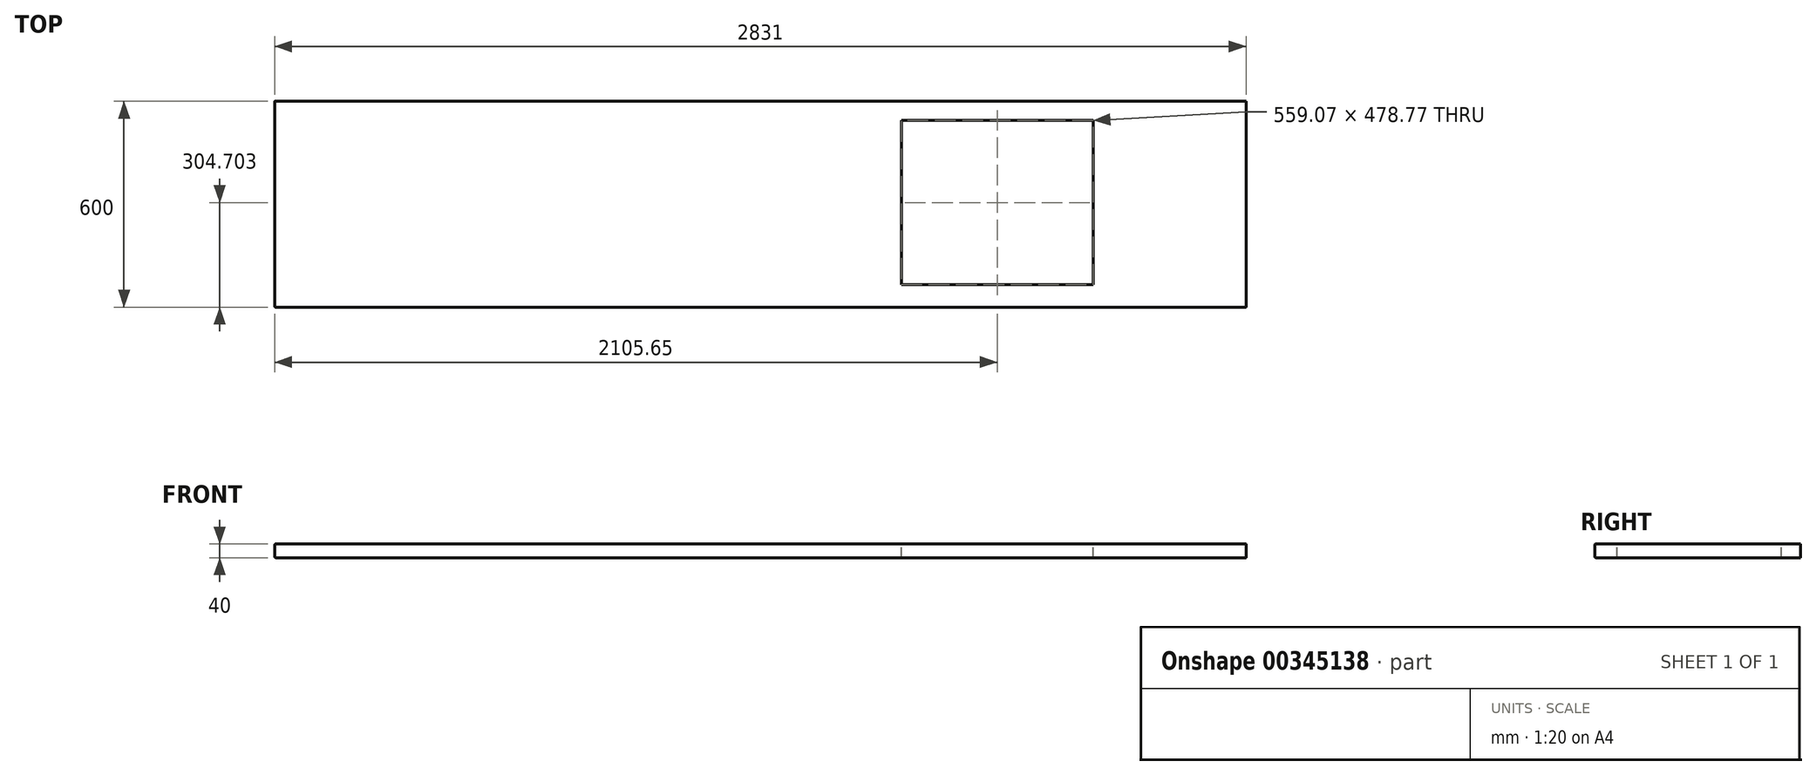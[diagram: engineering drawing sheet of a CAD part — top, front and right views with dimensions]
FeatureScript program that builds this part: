
annotation { "Feature Type Name" : "Feature", "Feature Type Description" : "" }
export const myFeature = defineFeature(function(context is Context, id is Id, definition is map)
    precondition{}
    {
        {
            var Q0;
            Q0=qCreatedBy(makeId("Top.planeOp"),FACE);
            var sketch = newSketch(context, id + "F0", { "sketchPlane" : qUnion([Q0])});
            skLineSegment(sketch, "E0.bottom", {"start": v(0, 0) * mm, "end": v(45.3, 0) * mm});
            skLineSegment(sketch, "E0.top", {"start": v(0, -35.35) * mm, "end": v(45.3, -35.35) * mm});
            skLineSegment(sketch, "E0.left", {"start": v(0, 0) * mm, "end": v(0, -35.35) * mm});
            skLineSegment(sketch, "E0.right", {"start": v(45.3, 0) * mm, "end": v(45.3, -35.35) * mm});
            skSolve(sketch);
        }
        {
            var Q0;
            Q0=makeQuery(id+"F0.imprint","IMPRINT",FACE,{"disambiguationData":[TD([[makeQuery(id+"F0.imprint","IMPRINT",EDGE,{"derivedFrom":sQuery(id+"F0.wireOp",EDGE,"E0.bottom")}),-1.0]])]});
            extrude(context, id + "F1", {"entities" : qUnion([Q0]), "depth" : 40 * mm});
        }
        {
            var Q0;
            Q0=makeQuery(id+"F1.opExtrude","SWEPT_FACE",FACE,{"disambiguationData":[OSD([sQuery(id+"F0.wireOp",EDGE,"E0.left")])]});
            extrude(context, id + "F2", {"entities" : qUnion([Q0]), "operationType" : NewBodyOperationType.ADD, "oppositeDirection" : true, "depth" : 2900 * mm});
        }
        {
            var Q0;
            {var subQ0=sQuery(id+"F0.wireOp",EDGE,"E0.bottom");Q0=makeQuery(id+"F2.boolean.opBoolean","MERGE",FACE,{"derivedFrom":[makeQuery(id+"F1.opExtrude","SWEPT_FACE",FACE,{"disambiguationData":[OSD([subQ0])]}),makeQuery(id+"F2.opExtrude","SWEPT_FACE",FACE,{"disambiguationData":[OSD([subQ0,sQuery(id+"F0.wireOp",EDGE,"E0.left")])]})]});}
            extrude(context, id + "F3", {"entities" : qUnion([Q0]), "operationType" : NewBodyOperationType.ADD, "oppositeDirection" : true, "depth" : 600 * mm});
        }
        {
            var Q0;
            {var subQ0=sQuery(id+"F0.wireOp",EDGE,"E0.left");var subQ1=sQuery(id+"F0.wireOp",EDGE,"E0.bottom");Q0=makeQuery(id+"F3.boolean.opBoolean","MERGE",FACE,{"derivedFrom":[makeQuery(id+"F1.opExtrude","SWEPT_FACE",FACE,{"disambiguationData":[OSD([subQ0])]}),makeQuery(id+"F3.opExtrude","SWEPT_FACE",FACE,{"disambiguationData":[OSD([subQ1,subQ0]),TDD([makeQuery(id+"F1.opExtrude","SWEPT_EDGE",EDGE,{"disambiguationData":[OSD([subQ1,subQ0])]})])]})]});}
            extrude(context, id + "F4", {"entities" : qUnion([Q0]), "operationType" : NewBodyOperationType.ADD, "oppositeDirection" : true, "depth" : 2850 * mm});
        }
        {
            var Q0;
            {var subQ0=sQuery(id+"F0.wireOp",EDGE,"E0.left");var subQ1=sQuery(id+"F0.wireOp",EDGE,"E0.bottom");Q0=makeQuery(id+"F3.boolean.opBoolean","MERGE",FACE,{"derivedFrom":[makeQuery(id+"F2.opExtrude","CAP_FACE",FACE,{"disambiguationData":[OSD([subQ0])],"isStart":false}),makeQuery(id+"F3.opExtrude","SWEPT_FACE",FACE,{"disambiguationData":[OSD([subQ1,subQ0]),TDD([makeQuery(id+"F2.opExtrude","CAP_EDGE",EDGE,{"disambiguationData":[OSD([subQ1,subQ0])],"isStart":false})])]})]});}
            extrude(context, id + "F5", {"entities" : qUnion([Q0]), "operationType" : NewBodyOperationType.REMOVE, "oppositeDirection" : true, "depth" : 50 * mm});
        }
        {
            var Q0;
            Q0=makeQuery(id+"F5.boolean.opBoolean","COPY",FACE,{"derivedFrom":makeQuery(id+"F5.opExtrude","CAP_FACE",FACE,{"disambiguationData":[OSD([sQuery(id+"F0.wireOp",EDGE,"E0.bottom"),sQuery(id+"F0.wireOp",EDGE,"E0.left")])],"isStart":false})});
            extrude(context, id + "F6", {"entities" : qUnion([Q0]), "operationType" : NewBodyOperationType.REMOVE, "oppositeDirection" : true, "depth" : 25 * mm});
        }
        {
            var Q0;
            Q0=makeQuery(id+"F6.boolean.opBoolean","COPY",FACE,{"derivedFrom":makeQuery(id+"F6.opExtrude","CAP_FACE",FACE,{"disambiguationData":[OSD([sQuery(id+"F0.wireOp",EDGE,"E0.bottom"),sQuery(id+"F0.wireOp",EDGE,"E0.left")])],"isStart":false})});
            extrude(context, id + "F7", {"entities" : qUnion([Q0]), "operationType" : NewBodyOperationType.ADD, "depth" : 10 * mm});
        }
        {
            var Q0;
            Q0=makeQuery(id+"F7.opExtrude","CAP_FACE",FACE,{"disambiguationData":[OSD([sQuery(id+"F0.wireOp",EDGE,"E0.bottom"),sQuery(id+"F0.wireOp",EDGE,"E0.left")])],"isStart":false});
            extrude(context, id + "F8", {"entities" : qUnion([Q0]), "operationType" : NewBodyOperationType.REMOVE, "oppositeDirection" : true, "depth" : 5 * mm});
        }
        {
            var Q0;
            Q0=makeQuery(id+"F8.boolean.opBoolean","COPY",FACE,{"derivedFrom":makeQuery(id+"F8.opExtrude","CAP_FACE",FACE,{"disambiguationData":[OSD([sQuery(id+"F0.wireOp",EDGE,"E0.bottom"),sQuery(id+"F0.wireOp",EDGE,"E0.left")])],"isStart":false})});
            extrude(context, id + "F9", {"entities" : qUnion([Q0]), "operationType" : NewBodyOperationType.ADD, "depth" : 2 * mm});
        }
        {
            var Q0;
            Q0=makeQuery(id+"F9.opExtrude","CAP_FACE",FACE,{"disambiguationData":[OSD([sQuery(id+"F0.wireOp",EDGE,"E0.bottom"),sQuery(id+"F0.wireOp",EDGE,"E0.left")])],"isStart":false});
            extrude(context, id + "F10", {"entities" : qUnion([Q0]), "operationType" : NewBodyOperationType.REMOVE, "oppositeDirection" : true, "depth" : 1 * mm});
        }
        {
            var Q0;
            {var subQ0=sQuery(id+"F0.wireOp",EDGE,"E0.left");var subQ1=sQuery(id+"F0.wireOp",EDGE,"E0.bottom");var subQ2=makeQuery(id+"F1.opExtrude","CAP_VERTEX",VERTEX,{"disambiguationData":[OSD([subQ1,subQ0])],"isStart":false});var subQ3=makeQuery(id+"F6.boolean.opBoolean","COPY",VERTEX,{"derivedFrom":makeQuery(id+"F6.opExtrude","CAP_VERTEX",VERTEX,{"disambiguationData":[OSD([subQ1,subQ0]),TDD([makeQuery(id+"F5.boolean.opBoolean","COPY",VERTEX,{"derivedFrom":makeQuery(id+"F5.opExtrude","CAP_VERTEX",VERTEX,{"disambiguationData":[OSD([subQ1,subQ0]),TDD([makeQuery(id+"F3.opExtrude","CAP_VERTEX",VERTEX,{"disambiguationData":[OSD([subQ1,subQ0]),TDD([makeQuery(id+"F2.opExtrude","CAP_VERTEX",VERTEX,{"disambiguationData":[OSD([subQ1,subQ0]),TDD([subQ2])],"isStart":false})])],"isStart":false})])],"isStart":false})})])],"isStart":false})});Q0=makeQuery(id+"F9.boolean.opBoolean","MERGE",EDGE,{"derivedFrom":[makeQuery(id+"F7.boolean.opBoolean","MERGE",EDGE,{"derivedFrom":[makeQuery(id+"F3.opExtrude","CAP_EDGE",EDGE,{"disambiguationData":[OSD([subQ1,subQ0]),TDD([makeQuery(id+"F2.boolean.opBoolean","MERGE",EDGE,{"derivedFrom":[makeQuery(id+"F1.opExtrude","CAP_EDGE",EDGE,{"disambiguationData":[OSD([subQ1])],"isStart":false}),makeQuery(id+"F2.opExtrude","SWEPT_EDGE",EDGE,{"disambiguationData":[OSD([subQ1,subQ0]),TDD([subQ2])]})]})])],"isStart":false}),makeQuery(id+"F7.opExtrude","SWEPT_EDGE",EDGE,{"disambiguationData":[OSD([subQ1,subQ0]),TDD([subQ3])]})]}),makeQuery(id+"F9.opExtrude","SWEPT_EDGE",EDGE,{"disambiguationData":[OSD([subQ1,subQ0]),TDD([makeQuery(id+"F8.boolean.opBoolean","COPY",VERTEX,{"derivedFrom":makeQuery(id+"F8.opExtrude","CAP_VERTEX",VERTEX,{"disambiguationData":[OSD([subQ1,subQ0]),TDD([makeQuery(id+"F7.opExtrude","CAP_VERTEX",VERTEX,{"disambiguationData":[OSD([subQ1,subQ0]),TDD([subQ3])],"isStart":false})])],"isStart":false})})])]})]});}
            var Q1;
            {var subQ0=sQuery(id+"F0.wireOp",EDGE,"E0.left");var subQ1=sQuery(id+"F0.wireOp",EDGE,"E0.bottom");Q1=makeQuery(id+"F3.boolean.opBoolean","MERGE",EDGE,{"derivedFrom":[makeQuery(id+"F1.opExtrude","CAP_EDGE",EDGE,{"disambiguationData":[OSD([subQ0])],"isStart":false}),makeQuery(id+"F3.opExtrude","SWEPT_EDGE",EDGE,{"disambiguationData":[OSD([subQ1,subQ0]),TDD([makeQuery(id+"F1.opExtrude","CAP_VERTEX",VERTEX,{"disambiguationData":[OSD([subQ1,subQ0])],"isStart":false})])]})]});}
            var Q2;
            {var subQ0=sQuery(id+"F0.wireOp",EDGE,"E0.left");var subQ1=sQuery(id+"F0.wireOp",EDGE,"E0.bottom");Q2=makeQuery(id+"F3.opExtrude","CAP_EDGE",EDGE,{"disambiguationData":[OSD([subQ1,subQ0]),TDD([makeQuery(id+"F1.opExtrude","SWEPT_EDGE",EDGE,{"disambiguationData":[OSD([subQ1,subQ0])]})])],"isStart":false});}
            var Q3;
            {var subQ0=sQuery(id+"F0.wireOp",EDGE,"E0.left");var subQ1=sQuery(id+"F0.wireOp",EDGE,"E0.bottom");var subQ2=makeQuery(id+"F1.opExtrude","CAP_VERTEX",VERTEX,{"disambiguationData":[OSD([subQ1,subQ0])],"isStart":true});var subQ3=makeQuery(id+"F6.boolean.opBoolean","COPY",VERTEX,{"derivedFrom":makeQuery(id+"F6.opExtrude","CAP_VERTEX",VERTEX,{"disambiguationData":[OSD([subQ1,subQ0]),TDD([makeQuery(id+"F5.boolean.opBoolean","COPY",VERTEX,{"derivedFrom":makeQuery(id+"F5.opExtrude","CAP_VERTEX",VERTEX,{"disambiguationData":[OSD([subQ1,subQ0]),TDD([makeQuery(id+"F3.opExtrude","CAP_VERTEX",VERTEX,{"disambiguationData":[OSD([subQ1,subQ0]),TDD([makeQuery(id+"F2.opExtrude","CAP_VERTEX",VERTEX,{"disambiguationData":[OSD([subQ1,subQ0]),TDD([subQ2])],"isStart":false})])],"isStart":false})])],"isStart":false})})])],"isStart":false})});Q3=makeQuery(id+"F9.boolean.opBoolean","MERGE",EDGE,{"derivedFrom":[makeQuery(id+"F7.boolean.opBoolean","MERGE",EDGE,{"derivedFrom":[makeQuery(id+"F3.opExtrude","CAP_EDGE",EDGE,{"disambiguationData":[OSD([subQ1,subQ0]),TDD([makeQuery(id+"F2.boolean.opBoolean","MERGE",EDGE,{"derivedFrom":[makeQuery(id+"F1.opExtrude","CAP_EDGE",EDGE,{"disambiguationData":[OSD([subQ1])],"isStart":true}),makeQuery(id+"F2.opExtrude","SWEPT_EDGE",EDGE,{"disambiguationData":[OSD([subQ1,subQ0]),TDD([subQ2])]})]})])],"isStart":false}),makeQuery(id+"F7.opExtrude","SWEPT_EDGE",EDGE,{"disambiguationData":[OSD([subQ1,subQ0]),TDD([subQ3])]})]}),makeQuery(id+"F9.opExtrude","SWEPT_EDGE",EDGE,{"disambiguationData":[OSD([subQ1,subQ0]),TDD([makeQuery(id+"F8.boolean.opBoolean","COPY",VERTEX,{"derivedFrom":makeQuery(id+"F8.opExtrude","CAP_VERTEX",VERTEX,{"disambiguationData":[OSD([subQ1,subQ0]),TDD([makeQuery(id+"F7.opExtrude","CAP_VERTEX",VERTEX,{"disambiguationData":[OSD([subQ1,subQ0]),TDD([subQ3])],"isStart":false})])],"isStart":false})})])]})]});}
            var Q4;
            {var subQ0=sQuery(id+"F0.wireOp",EDGE,"E0.left");var subQ1=sQuery(id+"F0.wireOp",EDGE,"E0.bottom");Q4=makeQuery(id+"F3.boolean.opBoolean","MERGE",EDGE,{"derivedFrom":[makeQuery(id+"F1.opExtrude","CAP_EDGE",EDGE,{"disambiguationData":[OSD([subQ0])],"isStart":true}),makeQuery(id+"F3.opExtrude","SWEPT_EDGE",EDGE,{"disambiguationData":[OSD([subQ1,subQ0]),TDD([makeQuery(id+"F1.opExtrude","CAP_VERTEX",VERTEX,{"disambiguationData":[OSD([subQ1,subQ0])],"isStart":true})])]})]});}
            fillet(context, id + "F11", {"entities" : qUnion([Q0, Q1, Q2, Q3, Q4]), "radius" : 3 * mm, "tangentPropagation" : true, "allowEdgeOverflow" : false});
        }
        {
            var Q0;
            {var subQ0=sQuery(id+"F0.wireOp",EDGE,"E0.left");var subQ1=sQuery(id+"F0.wireOp",EDGE,"E0.bottom");var subQ2=makeQuery(id+"F1.opExtrude","CAP_VERTEX",VERTEX,{"disambiguationData":[OSD([subQ1,subQ0])],"isStart":false});var subQ3=makeQuery(id+"F1.opExtrude","CAP_EDGE",EDGE,{"disambiguationData":[OSD([subQ0])],"isStart":false});var subQ4=makeQuery(id+"F6.boolean.opBoolean","COPY",EDGE,{"derivedFrom":makeQuery(id+"F6.opExtrude","CAP_EDGE",EDGE,{"disambiguationData":[OSD([subQ1,subQ0]),TDD([makeQuery(id+"F5.boolean.opBoolean","COPY",EDGE,{"derivedFrom":makeQuery(id+"F5.opExtrude","CAP_EDGE",EDGE,{"disambiguationData":[OSD([subQ1,subQ0]),TDD([makeQuery(id+"F3.boolean.opBoolean","MERGE",EDGE,{"derivedFrom":[makeQuery(id+"F2.opExtrude","CAP_EDGE",EDGE,{"disambiguationData":[OSD([subQ0]),TDD([subQ3])],"isStart":false}),makeQuery(id+"F3.opExtrude","SWEPT_EDGE",EDGE,{"disambiguationData":[OSD([subQ1,subQ0]),TDD([makeQuery(id+"F2.opExtrude","CAP_VERTEX",VERTEX,{"disambiguationData":[OSD([subQ1,subQ0]),TDD([subQ2])],"isStart":false})])]})]})])],"isStart":false})})])],"isStart":false})});Q0=makeQuery(id+"F9.boolean.opBoolean","MERGE",FACE,{"derivedFrom":[makeQuery(id+"F7.boolean.opBoolean","MERGE",FACE,{"derivedFrom":[makeQuery(id+"F3.boolean.opBoolean","MERGE",FACE,{"derivedFrom":[makeQuery(id+"F2.boolean.opBoolean","MERGE",FACE,{"derivedFrom":[makeQuery(id+"F1.opExtrude","CAP_FACE",FACE,{"disambiguationData":[OSD([subQ1,sQuery(id+"F0.wireOp",EDGE,"E0.top"),subQ0,sQuery(id+"F0.wireOp",EDGE,"E0.right")])],"isStart":false}),makeQuery(id+"F2.opExtrude","SWEPT_FACE",FACE,{"disambiguationData":[OSD([subQ0]),TDD([subQ3])]})]}),makeQuery(id+"F3.opExtrude","SWEPT_FACE",FACE,{"disambiguationData":[OSD([subQ1,subQ0]),TDD([makeQuery(id+"F2.boolean.opBoolean","MERGE",EDGE,{"derivedFrom":[makeQuery(id+"F1.opExtrude","CAP_EDGE",EDGE,{"disambiguationData":[OSD([subQ1])],"isStart":false}),makeQuery(id+"F2.opExtrude","SWEPT_EDGE",EDGE,{"disambiguationData":[OSD([subQ1,subQ0]),TDD([subQ2])]})]})])]})]}),makeQuery(id+"F7.opExtrude","SWEPT_FACE",FACE,{"disambiguationData":[OSD([subQ1,subQ0]),TDD([subQ4])]})]}),makeQuery(id+"F9.opExtrude","SWEPT_FACE",FACE,{"disambiguationData":[OSD([subQ1,subQ0]),TDD([makeQuery(id+"F8.boolean.opBoolean","COPY",EDGE,{"derivedFrom":makeQuery(id+"F8.opExtrude","CAP_EDGE",EDGE,{"disambiguationData":[OSD([subQ1,subQ0]),TDD([makeQuery(id+"F7.opExtrude","CAP_EDGE",EDGE,{"disambiguationData":[OSD([subQ1,subQ0]),TDD([subQ4])],"isStart":false})])],"isStart":false})})])]})]});}
            var sketch = newSketch(context, id + "F12", { "sketchPlane" : qUnion([Q0])});
            skLineSegment(sketch, "E1.bottom", {"start": v(2126.12, -110.91) * mm, "end": v(2685.2, -110.91) * mm});
            skLineSegment(sketch, "E1.top", {"start": v(2126.12, -494.68) * mm, "end": v(2685.2, -494.68) * mm});
            skLineSegment(sketch, "E1.left", {"start": v(2126.12, -110.91) * mm, "end": v(2126.12, -494.68) * mm});
            skLineSegment(sketch, "E1.right", {"start": v(2685.2, -110.91) * mm, "end": v(2685.2, -494.68) * mm});
            skSolve(sketch);
        }
        {
            var Q0;
            Q0=makeQuery(id+"F12.imprint","IMPRINT",FACE,{"disambiguationData":[TD([[makeQuery(id+"F12.imprint","IMPRINT",EDGE,{"derivedFrom":sQuery(id+"F12.wireOp",EDGE,"E1.bottom")}),-1.0]])]});
            extrude(context, id + "F13", {"entities" : qUnion([Q0]), "operationType" : NewBodyOperationType.REMOVE, "oppositeDirection" : true, "depth" : 40 * mm});
        }
        {
            var Q0;
            Q0=makeQuery(id+"F13.boolean.opBoolean","COPY",FACE,{"derivedFrom":makeQuery(id+"F13.opExtrude","SWEPT_FACE",FACE,{"disambiguationData":[OSD([sQuery(id+"F12.wireOp",EDGE,"E1.top")])]})});
            extrude(context, id + "F14", {"entities" : qUnion([Q0]), "operationType" : NewBodyOperationType.REMOVE, "oppositeDirection" : true, "depth" : 40 * mm});
        }
        {
            var Q0;
            Q0=makeQuery(id+"F13.boolean.opBoolean","COPY",FACE,{"derivedFrom":makeQuery(id+"F13.opExtrude","SWEPT_FACE",FACE,{"disambiguationData":[OSD([sQuery(id+"F12.wireOp",EDGE,"E1.bottom")])]})});
            extrude(context, id + "F15", {"entities" : qUnion([Q0]), "operationType" : NewBodyOperationType.REMOVE, "oppositeDirection" : true, "depth" : 25 * mm});
        }
        {
            var Q0;
            Q0=makeQuery(id+"F15.boolean.opBoolean","COPY",FACE,{"derivedFrom":makeQuery(id+"F15.opExtrude","CAP_FACE",FACE,{"disambiguationData":[OSD([sQuery(id+"F12.wireOp",EDGE,"E1.bottom")])],"isStart":false})});
            extrude(context, id + "F16", {"entities" : qUnion([Q0]), "operationType" : NewBodyOperationType.REMOVE, "oppositeDirection" : true, "depth" : 30 * mm});
        }
        {
            var Q0;
            {var subQ0=sQuery(id+"F12.wireOp",EDGE,"E1.left");var subQ1=sQuery(id+"F12.wireOp",EDGE,"E1.bottom");Q0=makeQuery(id+"F16.boolean.opBoolean","MERGE",FACE,{"derivedFrom":[makeQuery(id+"F15.boolean.opBoolean","MERGE",FACE,{"derivedFrom":[makeQuery(id+"F14.boolean.opBoolean","MERGE",FACE,{"derivedFrom":[makeQuery(id+"F13.boolean.opBoolean","COPY",FACE,{"derivedFrom":makeQuery(id+"F13.opExtrude","SWEPT_FACE",FACE,{"disambiguationData":[OSD([subQ0])]})}),makeQuery(id+"F14.opExtrude","SWEPT_FACE",FACE,{"disambiguationData":[OSD([sQuery(id+"F12.wireOp",EDGE,"E1.top"),subQ0])]})]}),makeQuery(id+"F15.opExtrude","SWEPT_FACE",FACE,{"disambiguationData":[OSD([subQ1,subQ0])]})]}),makeQuery(id+"F16.opExtrude","SWEPT_FACE",FACE,{"disambiguationData":[OSD([subQ1,subQ0])]})]});}
            extrude(context, id + "F17", {"entities" : qUnion([Q0]), "operationType" : NewBodyOperationType.REMOVE, "oppositeDirection" : true, "depth" : 400 * mm});
        }
        {
            var Q0;
            Q0=makeQuery(id+"F17.boolean.opBoolean","COPY",FACE,{"derivedFrom":makeQuery(id+"F17.opExtrude","CAP_FACE",FACE,{"disambiguationData":[OSD([sQuery(id+"F12.wireOp",EDGE,"E1.bottom"),sQuery(id+"F12.wireOp",EDGE,"E1.top"),sQuery(id+"F12.wireOp",EDGE,"E1.left")])],"isStart":false})});
            extrude(context, id + "F18", {"entities" : qUnion([Q0]), "operationType" : NewBodyOperationType.ADD, "depth" : 60 * mm});
        }
        {
            var Q0;
            Q0=makeQuery(id+"F18.opExtrude","CAP_FACE",FACE,{"disambiguationData":[OSD([sQuery(id+"F12.wireOp",EDGE,"E1.bottom"),sQuery(id+"F12.wireOp",EDGE,"E1.top"),sQuery(id+"F12.wireOp",EDGE,"E1.left")])],"isStart":false});
            extrude(context, id + "F19", {"entities" : qUnion([Q0]), "operationType" : NewBodyOperationType.ADD, "depth" : 40 * mm});
        }
        {
            var Q0;
            {var subQ0=sQuery(id+"F12.wireOp",EDGE,"E1.right");var subQ1=sQuery(id+"F12.wireOp",EDGE,"E1.bottom");Q0=makeQuery(id+"F16.boolean.opBoolean","MERGE",FACE,{"derivedFrom":[makeQuery(id+"F15.boolean.opBoolean","MERGE",FACE,{"derivedFrom":[makeQuery(id+"F14.boolean.opBoolean","MERGE",FACE,{"derivedFrom":[makeQuery(id+"F13.boolean.opBoolean","COPY",FACE,{"derivedFrom":makeQuery(id+"F13.opExtrude","SWEPT_FACE",FACE,{"disambiguationData":[OSD([subQ0])]})}),makeQuery(id+"F14.opExtrude","SWEPT_FACE",FACE,{"disambiguationData":[OSD([sQuery(id+"F12.wireOp",EDGE,"E1.top"),subQ0])]})]}),makeQuery(id+"F15.opExtrude","SWEPT_FACE",FACE,{"disambiguationData":[OSD([subQ1,subQ0])]})]}),makeQuery(id+"F16.opExtrude","SWEPT_FACE",FACE,{"disambiguationData":[OSD([subQ1,subQ0])]})]});}
            extrude(context, id + "F20", {"entities" : qUnion([Q0]), "operationType" : NewBodyOperationType.ADD, "depth" : 250 * mm});
        }
        {
            var Q0;
            Q0=makeQuery(id+"F20.opExtrude","CAP_FACE",FACE,{"disambiguationData":[OSD([sQuery(id+"F12.wireOp",EDGE,"E1.bottom"),sQuery(id+"F12.wireOp",EDGE,"E1.top"),sQuery(id+"F12.wireOp",EDGE,"E1.right")])],"isStart":false});
            extrude(context, id + "F21", {"entities" : qUnion([Q0]), "operationType" : NewBodyOperationType.ADD, "depth" : 50 * mm});
        }
    });
